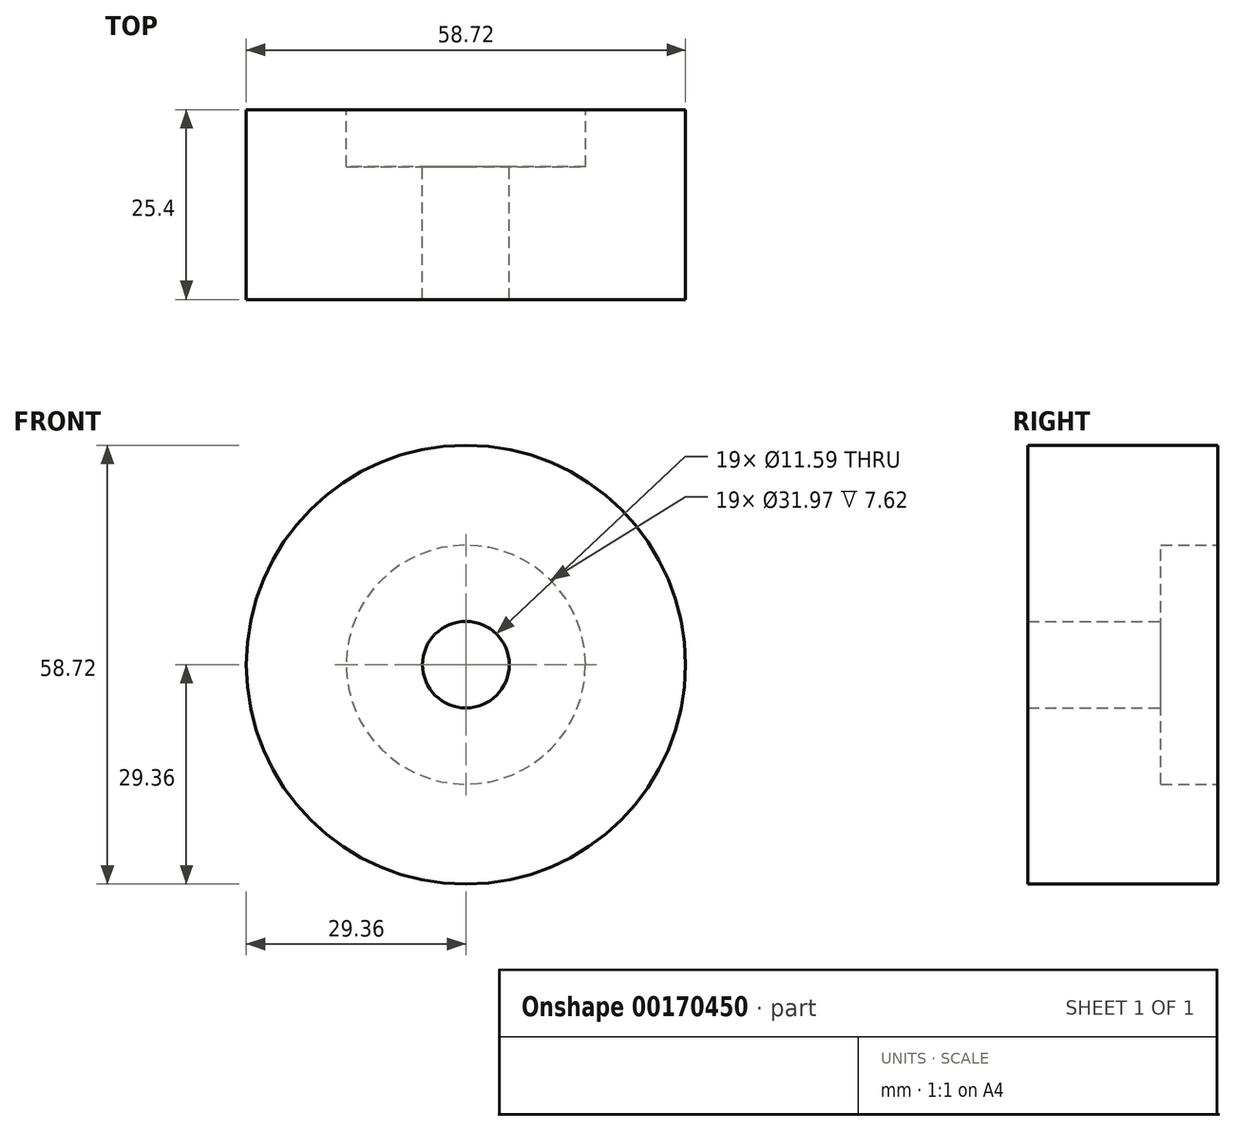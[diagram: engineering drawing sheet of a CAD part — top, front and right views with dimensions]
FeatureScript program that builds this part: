
annotation { "Feature Type Name" : "Feature", "Feature Type Description" : "" }
export const myFeature = defineFeature(function(context is Context, id is Id, definition is map)
    precondition{}
    {
        {
            var Q0;
            Q0=qCreatedBy(makeId("Front.planeOp"),FACE);
            var sketch = newSketch(context, id + "F0", { "sketchPlane" : qUnion([Q0])});
            skCircle(sketch, "E0", {"center": v(0, 0) * mm, "radius": 29.36 * mm});
            skCircle(sketch, "E1", {"center": v(0, 0) * mm, "radius": 15.99 * mm});
            skCircle(sketch, "E2", {"center": v(0, 0) * mm, "radius": 5.8 * mm});
            skSolve(sketch);
        }
        {
            var Q0;
            Q0 = qSketchRegion(id + "F0", true);
            var Q1;
            Q1=makeQuery(id+"F0.imprint","IMPRINT",FACE,{"disambiguationData":[TD([[makeQuery(id+"F0.imprint","IMPRINT",EDGE,{"derivedFrom":sQuery(id+"F0.wireOp",EDGE,"E1")}),1.0]])]});
            extrude(context, id + "F1", {"entities" : qUnion([Q0, Q1]), "depth" : 25.4 * mm});
        }
        {
            var Q0;
            Q0=makeQuery(id+"F0.imprint","IMPRINT",FACE,{"disambiguationData":[TD([[makeQuery(id+"F0.imprint","IMPRINT",EDGE,{"derivedFrom":sQuery(id+"F0.wireOp",EDGE,"E1")}),1.0]])]});
            extrude(context, id + "F2", {"entities" : qUnion([Q0]), "operationType" : NewBodyOperationType.REMOVE, "depth" : 7.62 * mm});
        }
    });
